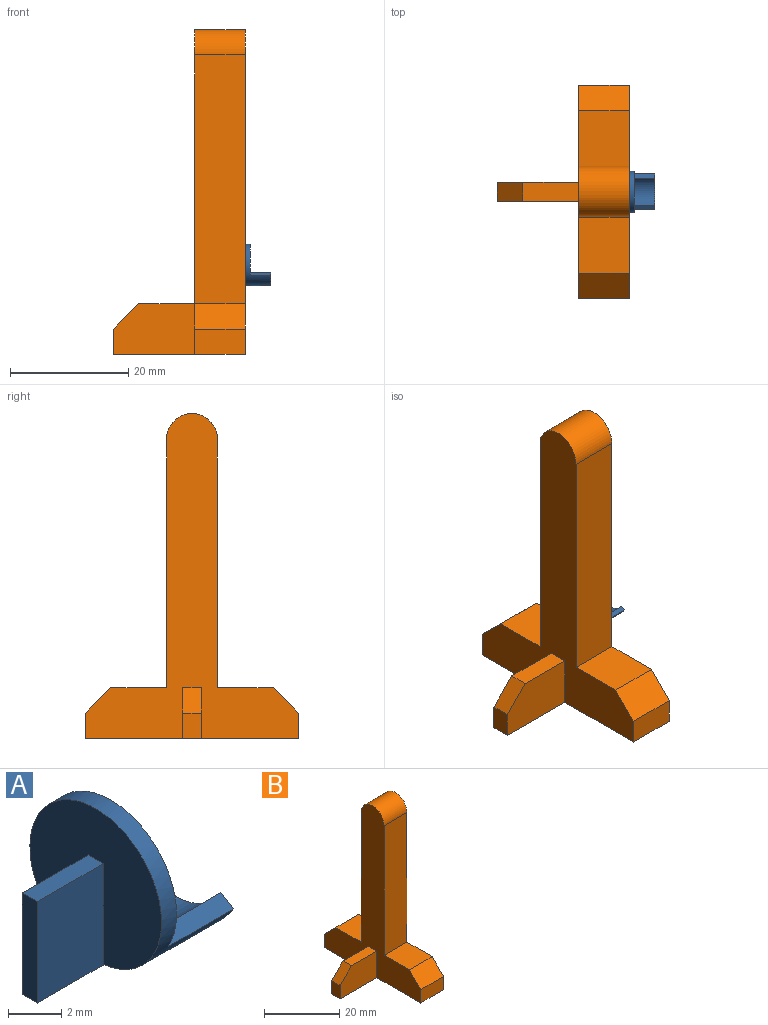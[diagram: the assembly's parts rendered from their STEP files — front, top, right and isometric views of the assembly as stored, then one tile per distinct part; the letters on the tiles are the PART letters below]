
ASSEMBLY  parts=2 mates=1
PART A: 14 faces, bbox 7.8x7x7 mm
  f0: plane 0.4x0.02mm, normal (1,0,0), area 0mm2, adj f2,f3,f8
  f1: plane 7x6.2mm, normal (1,0,0), area 33.3mm2, adj f8,f10,f11,f12
  f2: plane 4.67x4.3mm, normal (0,-1,0), area 16.4mm2, adj f0,f3,f5,f6,f8,f9
  f3: plane 4.3x0.8mm, normal (0,0,-1), area 3.4mm2, adj f0,f2,f4,f6,f7
  f4: plane 4.67x4.3mm, normal (0,1,0), area 16.4mm2, adj f3,f5,f6,f7,f8,f9
  f5: plane 3.5x0.8mm, normal (0,0,1), area 2.8mm2, adj f2,f4,f6,f9
  f6: plane 4.67x0.8mm, normal (-1,0,0), area 3.7mm2, adj f2,f3,f4,f5
  f7: plane 0.4x0.02mm, normal (1,0,0), area 0mm2, adj f3,f4,f8
  f8: cylinder r=3.5mm len=7mm, axis (1,0,0), area 42.6mm2, adj f0,f1,f2,f4,f7,f9,f10,f12
  f9: plane 7x6.98mm, normal (-1,0,0), area 34.8mm2, adj f2,f4,f5,f8
  f10: plane 3.5x0.69mm, normal (0,0.5,0.87), area 2.8mm2, adj f1,f8,f11,f13
  f11: cylinder r=2.7mm len=4.68mm, axis (-1,0,0), area 19.8mm2, adj f1,f10,f12,f13
  f12: plane 3.5x0.69mm, normal (0,-0.5,0.87), area 2.8mm2, adj f1,f8,f11,f13
  f13: plane 6.06x2.15mm, normal (1,0,0), area 5.2mm2, adj f8,f10,f11,f12
PART B: 37 faces, bbox 22.4x36.1x55 mm
  f0: plane 55x36.1mm, normal (1,0,0), area 662.4mm2, adj f2,f3,f4,f5,f6,f7,f8,f14
  f1: plane 55x36.1mm, normal (-1,0,0), area 655.6mm2, adj f2,f3,f4,f5,f6,f7,f8,f9
  f2: plane 42.1x8.6mm, normal (0,-1,0), area 362.1mm2, adj f0,f1,f6,f36
  f3: plane 42.1x8.6mm, normal (0,1,0), area 362.1mm2, adj f0,f1,f8,f36
  f4: plane 36.1x22.35mm, normal (0,0,-1), area 354.5mm2, adj f0,f1,f5,f7,f9,f10,f11
  f5: plane 8.6x4.3mm, normal (0,-1,0), area 37mm2, adj f0,f1,f4,f14
  f6: plane 9.45x8.6mm, normal (0,0,1), area 81.3mm2, adj f0,f1,f2,f14
  f7: plane 8.6x4.3mm, normal (0,1,0), area 37mm2, adj f0,f1,f4,f15
  f8: plane 9.45x8.6mm, normal (0,0,1), area 81.3mm2, adj f0,f1,f3,f15
  f9: plane 13.75x8.6mm, normal (0,1,0), area 109mm2, adj f1,f4,f10,f12,f13
  f10: plane 4.3x3.2mm, normal (-1,0,0), area 13.8mm2, adj f4,f9,f11,f13
  f11: plane 13.75x8.6mm, normal (0,-1,0), area 109mm2, adj f1,f4,f10,f12,f13
  f12: plane 9.45x3.2mm, normal (0,0,1), area 30.2mm2, adj f1,f9,f11,f13
  f13: plane 4.3x4.3mm, normal (-0.71,0,0.71), area 19.5mm2, adj f9,f10,f11,f12
  f14: plane 8.6x4.3mm, normal (0,-0.71,0.71), area 52.3mm2, adj f0,f1,f5,f6
  f15: plane 8.6x4.3mm, normal (0,0.71,0.71), area 52.3mm2, adj f0,f1,f7,f8
  f16: plane 3.75x1.05mm, normal (0,0,-1), area 3.9mm2, adj f0,f17,f19,f20
  f17: plane 4.92x3.75mm, normal (0,1,0), area 18.4mm2, adj f0,f16,f18,f20
  f18: plane 3.75x1.05mm, normal (0,0,1), area 3.9mm2, adj f0,f17,f19,f20
  f19: plane 4.92x3.75mm, normal (0,-1,0), area 18.4mm2, adj f0,f16,f18,f20
  f20: plane 4.92x1.05mm, normal (1,0,0), area 5.2mm2, adj f16,f17,f18,f19
  f21: plane 3.75x1.05mm, normal (0,0,1), area 3.9mm2, adj f0,f22,f24,f25
  f22: plane 4.92x3.75mm, normal (0,-1,0), area 18.4mm2, adj f0,f21,f23,f25
  f23: plane 3.75x1.05mm, normal (0,0,-1), area 3.9mm2, adj f0,f22,f24,f25
  f24: plane 4.92x3.75mm, normal (0,1,0), area 18.4mm2, adj f0,f21,f23,f25
  f25: plane 4.92x1.05mm, normal (1,0,0), area 5.2mm2, adj f21,f22,f23,f24
  f26: plane 3.75x1.05mm, normal (0,0,1), area 3.9mm2, adj f0,f27,f29,f30
  f27: plane 4.92x3.75mm, normal (0,-1,0), area 18.4mm2, adj f0,f26,f28,f30
  f28: plane 3.75x1.05mm, normal (0,0,-1), area 3.9mm2, adj f0,f27,f29,f30
  f29: plane 4.92x3.75mm, normal (0,1,0), area 18.4mm2, adj f0,f26,f28,f30
  f30: plane 4.92x1.05mm, normal (1,0,0), area 5.2mm2, adj f26,f27,f28,f29
  f31: plane 3.75x1.05mm, normal (0,0,1), area 3.9mm2, adj f0,f32,f34,f35
  f32: plane 4.92x3.75mm, normal (0,-1,0), area 18.4mm2, adj f0,f31,f33,f35
  f33: plane 3.75x1.05mm, normal (0,0,-1), area 3.9mm2, adj f0,f32,f34,f35
  f34: plane 4.92x3.75mm, normal (0,1,0), area 18.4mm2, adj f0,f31,f33,f35
  f35: plane 4.92x1.05mm, normal (1,0,0), area 5.2mm2, adj f31,f32,f33,f34
  f36: cylinder r=4.3mm len=8.6mm, axis (1,0,0), area 116.2mm2, adj f0,f1,f2,f3
PLACE A t=(0.8,-33.4,11.67)mm
PLACE B at identity fixed
MATE slider B.f0 <-> A.f9  axis (1,0,0) through (0,0,14)mm
